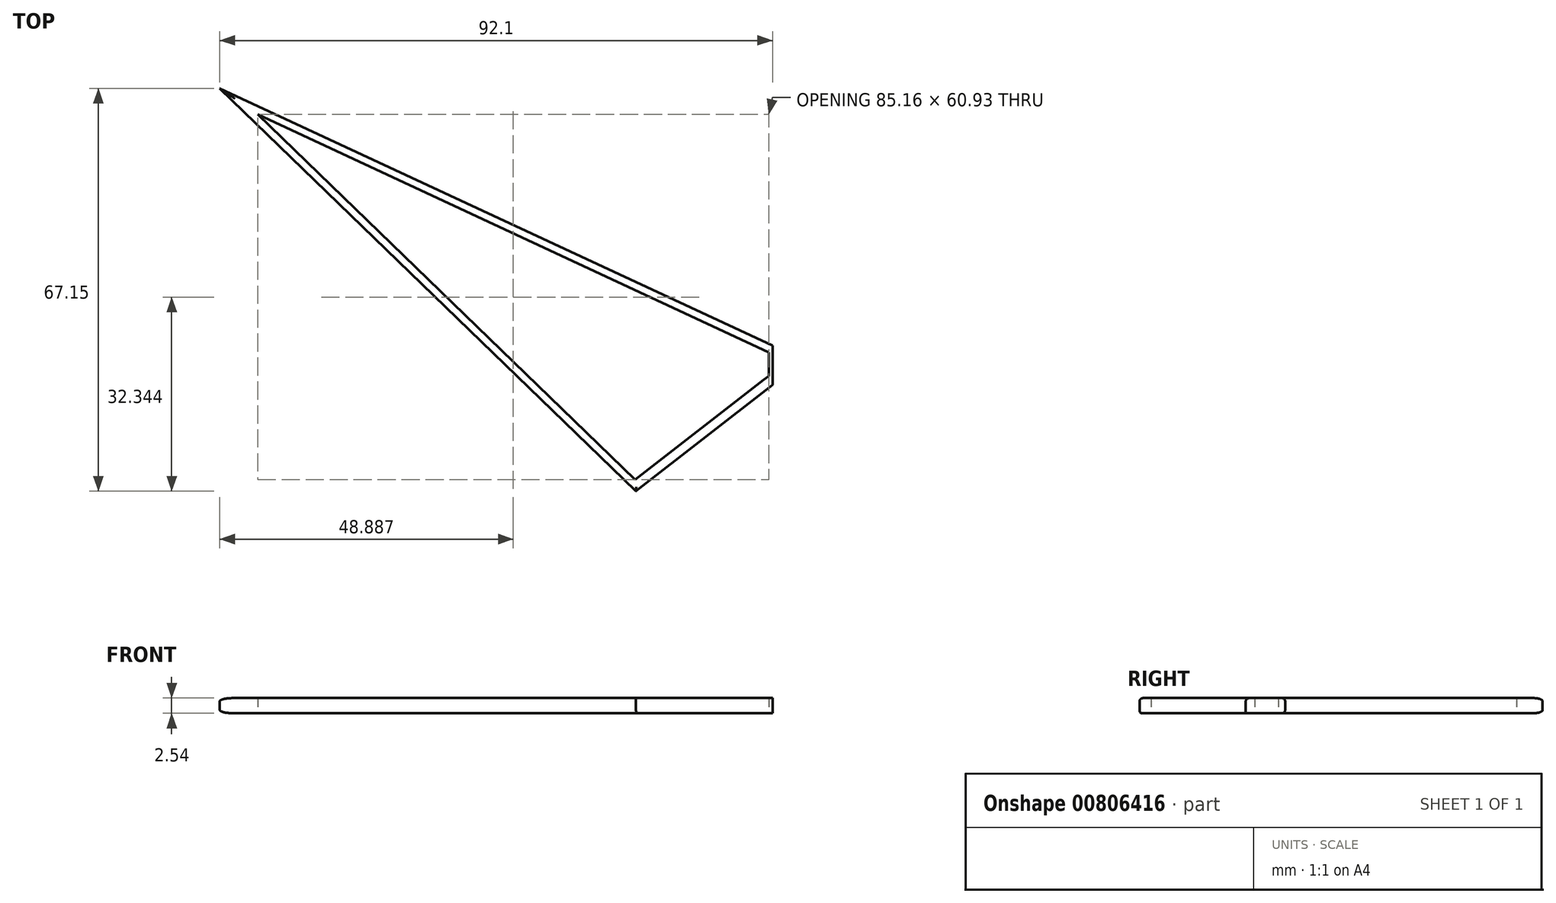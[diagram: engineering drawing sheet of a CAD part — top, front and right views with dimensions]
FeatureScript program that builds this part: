
annotation { "Feature Type Name" : "Feature", "Feature Type Description" : "" }
export const myFeature = defineFeature(function(context is Context, id is Id, definition is map)
    precondition{}
    {
        {
            var Q0;
            Q0=qCreatedBy(makeId("Top.planeOp"),FACE);
            var sketch = newSketch(context, id + "F0", { "sketchPlane" : qUnion([Q0])});
            skLineSegment(sketch, "E0", {"start": v(0, 0) * mm, "end": v(-22.76, -17.7) * mm});
            skLineSegment(sketch, "E1", {"start": v(-22.76, -17.7) * mm, "end": v(-92.1, 49.46) * mm});
            skLineSegment(sketch, "E2", {"start": v(-92.1, 49.46) * mm, "end": v(0, 6.55) * mm});
            skLineSegment(sketch, "E3", {"start": v(0, 0) * mm, "end": v(0, 6.55) * mm});
            skLineSegment(sketch, "E4", {"start": v(-0.64, 5.45) * mm, "end": v(-85.8, 45.12) * mm});
            skLineSegment(sketch, "E5", {"start": v(-85.8, 45.12) * mm, "end": v(-22.88, -15.8) * mm});
            skLineSegment(sketch, "E6", {"start": v(-22.88, -15.8) * mm, "end": v(-1.48, 0.83) * mm});
            skLineSegment(sketch, "E7", {"start": v(-0.64, 5.45) * mm, "end": v(-0.64, 1.49) * mm});
            skLineSegment(sketch, "E8", {"start": v(-0.64, 1.49) * mm, "end": v(-1.48, 0.83) * mm});
            skSolve(sketch);
        }
        {
            var Q0;
            Q0=makeQuery(id+"F0.imprint","IMPRINT",FACE,{"disambiguationData":[TD([[makeQuery(id+"F0.imprint","IMPRINT",EDGE,{"derivedFrom":sQuery(id+"F0.wireOp",EDGE,"E0")}),-1.0]])]});
            extrude(context, id + "F1", {"entities" : qUnion([Q0]), "depth" : 2.54 * mm, "offsetDistance" : 25.4 * mm});
        }
        {
            var Q0;
            Q0=makeQuery(id+"F1.opExtrude","CAP_EDGE",EDGE,{"disambiguationData":[OSD([sQuery(id+"F0.wireOp",EDGE,"E1")])],"isStart":false});
            var Q1;
            Q1=makeQuery(id+"F1.opExtrude","CAP_EDGE",EDGE,{"disambiguationData":[OSD([sQuery(id+"F0.wireOp",EDGE,"E0")])],"isStart":false});
            var Q2;
            Q2=makeQuery(id+"F1.opExtrude","CAP_EDGE",EDGE,{"disambiguationData":[OSD([sQuery(id+"F0.wireOp",EDGE,"E2")])],"isStart":false});
            var Q3;
            Q3=makeQuery(id+"F1.opExtrude","CAP_EDGE",EDGE,{"disambiguationData":[OSD([sQuery(id+"F0.wireOp",EDGE,"E2")])],"isStart":true});
            var Q4;
            Q4=makeQuery(id+"F1.opExtrude","CAP_EDGE",EDGE,{"disambiguationData":[OSD([sQuery(id+"F0.wireOp",EDGE,"E1")])],"isStart":true});
            fillet(context, id + "F2", {"entities" : qUnion([Q0, Q1, Q2, Q3, Q4]), "radius" : 0.5 * mm, "tangentPropagation" : true, "allowEdgeOverflow" : false});
        }
    });
